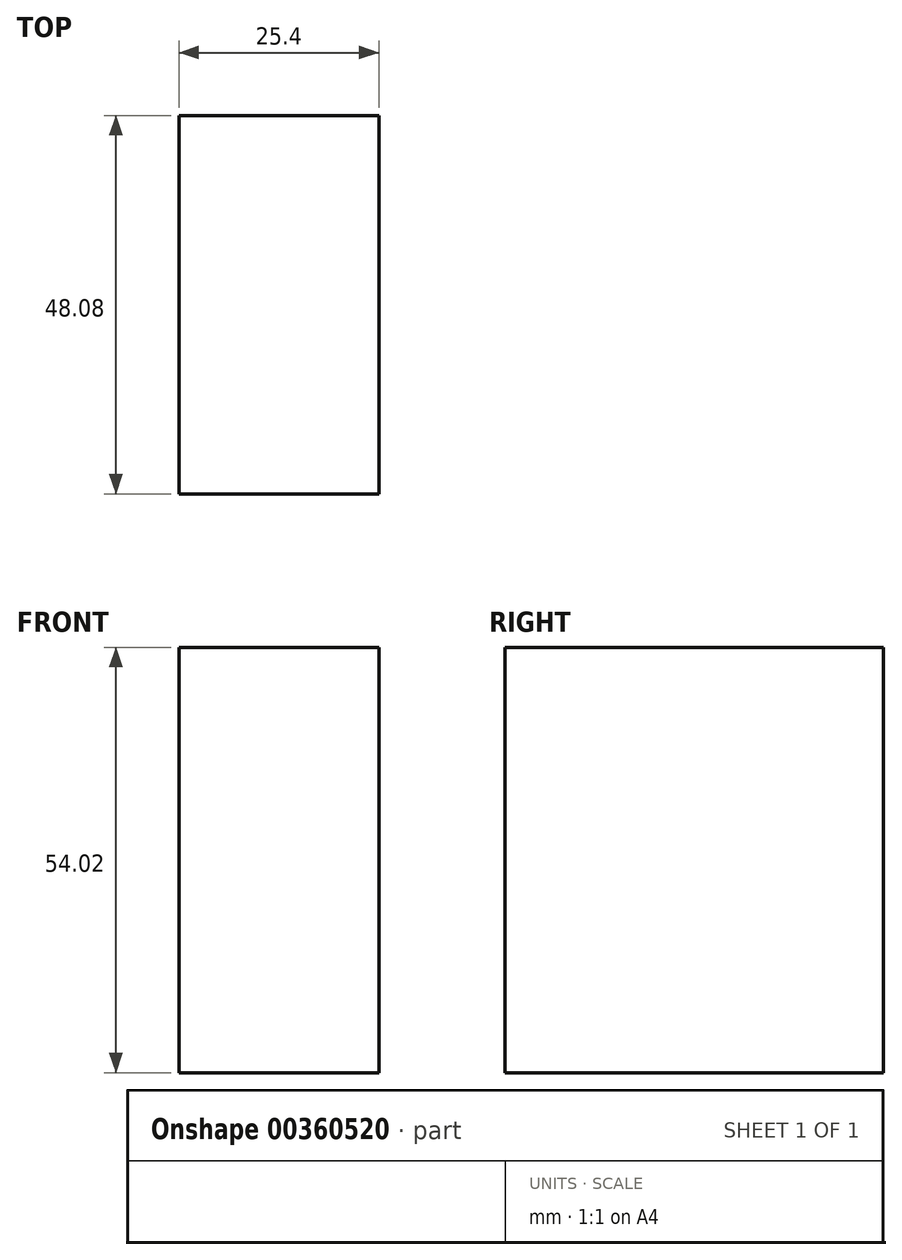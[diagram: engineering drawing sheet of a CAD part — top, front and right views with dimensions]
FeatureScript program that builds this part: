
annotation { "Feature Type Name" : "Feature", "Feature Type Description" : "" }
export const myFeature = defineFeature(function(context is Context, id is Id, definition is map)
    precondition{}
    {
        {
            var Q0;
            Q0=qCreatedBy(makeId("Right.planeOp"),FACE);
            var sketch = newSketch(context, id + "F0", { "sketchPlane" : qUnion([Q0])});
            skLineSegment(sketch, "E0.bottom", {"start": v(0, 0) * mm, "end": v(48.08, 0) * mm});
            skLineSegment(sketch, "E0.top", {"start": v(0, 54.02) * mm, "end": v(48.08, 54.02) * mm});
            skLineSegment(sketch, "E0.left", {"start": v(0, 0) * mm, "end": v(0, 54.02) * mm});
            skLineSegment(sketch, "E0.right", {"start": v(48.08, 0) * mm, "end": v(48.08, 54.02) * mm});
            skSolve(sketch);
        }
        {
            var Q0;
            Q0=makeQuery(id+"F0.imprint","IMPRINT",FACE,{"disambiguationData":[TD([[makeQuery(id+"F0.imprint","IMPRINT",EDGE,{"derivedFrom":sQuery(id+"F0.wireOp",EDGE,"E0.bottom")}),1.0]])]});
            extrude(context, id + "F1", {"entities" : qUnion([Q0]), "depth" : 25.4 * mm});
        }
    });
